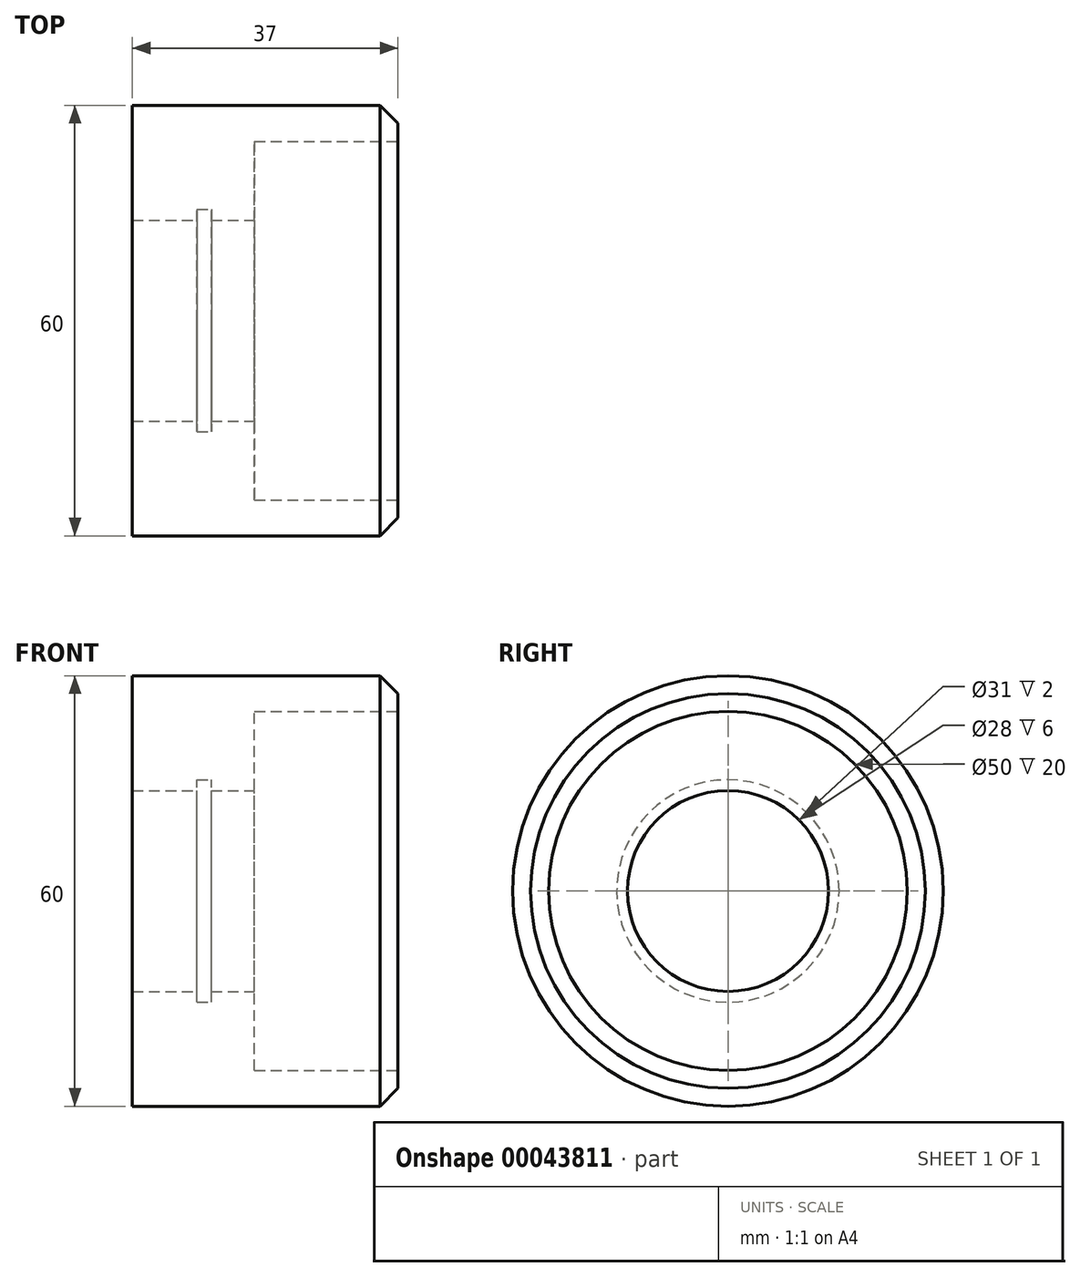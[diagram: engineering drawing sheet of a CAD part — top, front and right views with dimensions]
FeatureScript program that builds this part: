
annotation { "Feature Type Name" : "Feature", "Feature Type Description" : "" }
export const myFeature = defineFeature(function(context is Context, id is Id, definition is map)
    precondition{}
    {
        {
            var Q0;
            Q0=qCreatedBy(makeId("Front.planeOp"),FACE);
            var sketch = newSketch(context, id + "F0", { "sketchPlane" : qUnion([Q0])});
            skLineSegment(sketch, "E0", {"start": v(0, 0) * mm, "end": v(0, 30) * mm});
            skLineSegment(sketch, "E1", {"start": v(0, 30) * mm, "end": v(37, 30) * mm});
            skLineSegment(sketch, "E2", {"start": v(37, 30) * mm, "end": v(37, 0) * mm});
            skLineSegment(sketch, "E3", {"start": v(37, 0) * mm, "end": v(0, 0) * mm});
            skLineSegment(sketch, "E4", {"start": v(37, 25) * mm, "end": v(17, 25) * mm});
            skLineSegment(sketch, "E5", {"start": v(17, 25) * mm, "end": v(17, 14) * mm});
            skLineSegment(sketch, "E6", {"start": v(17, 14) * mm, "end": v(11, 14) * mm});
            skLineSegment(sketch, "E7", {"start": v(11, 14) * mm, "end": v(11, 15.5) * mm});
            skLineSegment(sketch, "E8", {"start": v(11, 15.5) * mm, "end": v(9, 15.5) * mm});
            skLineSegment(sketch, "E9", {"start": v(9, 15.5) * mm, "end": v(9, 14) * mm});
            skLineSegment(sketch, "E10", {"start": v(9, 14) * mm, "end": v(0, 14) * mm});
            skSolve(sketch);
        }
        {
            var Q0;
            {var subQ2=sQuery(id+"F0.wireOp",EDGE,"E1");Q0=makeQuery(id+"F0.imprint","IMPRINT",FACE,{"disambiguationData":[TD([[makeQuery(id+"F0.imprint","IMPRINT",EDGE,{"derivedFrom":subQ2}),-1.0]])]});}
            var Q1;
            Q1=sQuery(id+"F0.wireOp",EDGE,"E3");
            revolve(context, id + "F1", {"entities" : qUnion([Q0]), "axis" : qUnion([Q1]), "revolveType" : RevolveType.FULL});
        }
        {
            var Q0;
            Q0=makeQuery(id+"F1.opRevolve","SWEPT_EDGE",EDGE,{"disambiguationData":[OSD([sQuery(id+"F0.wireOp",EDGE,"E1"),sQuery(id+"F0.wireOp",EDGE,"E2")])]});
            chamfer(context, id + "F2", {"entities" : qUnion([Q0]), "width" : 2.5 * mm, "tangentPropagation" : true});
        }
    });
